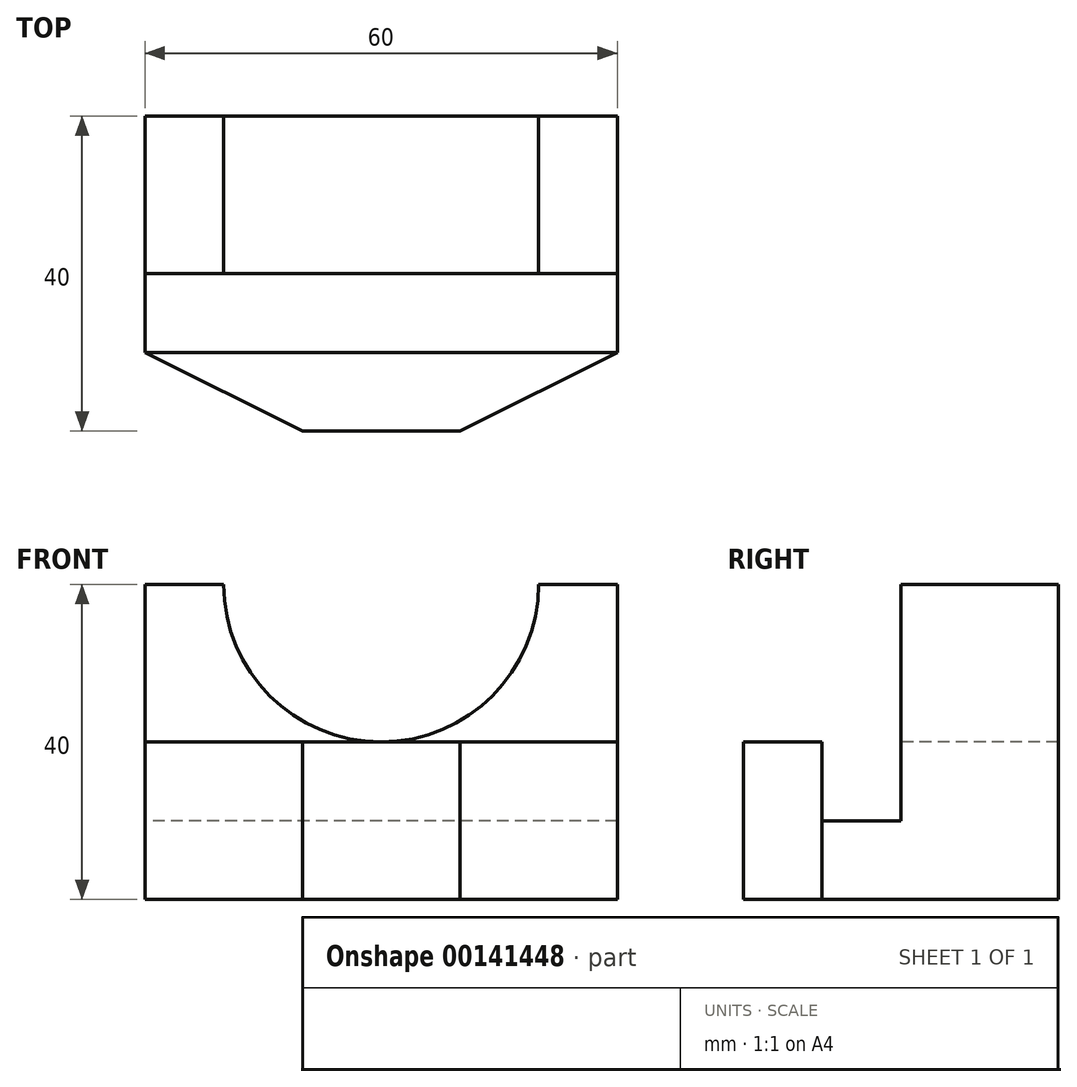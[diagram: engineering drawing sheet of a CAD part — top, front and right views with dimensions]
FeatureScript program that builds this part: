
annotation { "Feature Type Name" : "Feature", "Feature Type Description" : "" }
export const myFeature = defineFeature(function(context is Context, id is Id, definition is map)
    precondition{}
    {
        {
            var Q0;
            Q0=qCreatedBy(makeId("Front.planeOp"),FACE);
            var sketch = newSketch(context, id + "F0", { "sketchPlane" : qUnion([Q0])});
            skLineSegment(sketch, "E0.bottom", {"start": v(-30, 40) * mm, "end": v(30, 40) * mm});
            skLineSegment(sketch, "E0.top", {"start": v(-30, 0) * mm, "end": v(30, 0) * mm});
            skLineSegment(sketch, "E0.left", {"start": v(-30, 40) * mm, "end": v(-30, 0) * mm});
            skLineSegment(sketch, "E0.right", {"start": v(30, 40) * mm, "end": v(30, 0) * mm});
            skPoint(sketch, "E1", {"position": v(0, 40) * mm});
            skSolve(sketch);
        }
        {
            var Q0;
            Q0 = qSketchRegion(id + "F0", true);
            extrude(context, id + "F1", {"entities" : qUnion([Q0]), "oppositeDirection" : true, "depth" : 40 * mm});
        }
        {
            var Q0;
            Q0=makeQuery(id+"F1.opExtrude","SWEPT_FACE",FACE,{"disambiguationData":[OSD([sQuery(id+"F0.wireOp",EDGE,"E0.bottom")])]});
            var sketch = newSketch(context, id + "F2", { "sketchPlane" : qUnion([Q0])});
            skLineSegment(sketch, "E2", {"start": v(10, 0) * mm, "end": v(30, 10) * mm});
            skLineSegment(sketch, "E3", {"start": v(30, 10) * mm, "end": v(30, 0) * mm});
            skLineSegment(sketch, "E4", {"start": v(30, 0) * mm, "end": v(10, 0) * mm});
            skLineSegment(sketch, "E5", {"start": v(-30, 10) * mm, "end": v(-10, 0) * mm});
            skLineSegment(sketch, "E6", {"start": v(-10, 0) * mm, "end": v(-30, 0) * mm});
            skLineSegment(sketch, "E7", {"start": v(-30, 0) * mm, "end": v(-30, 10) * mm});
            skSolve(sketch);
        }
        {
            var Q0;
            Q0 = qSketchRegion(id + "F2", true);
            extrude(context, id + "F3", {"entities" : qUnion([Q0]), "operationType" : NewBodyOperationType.REMOVE, "endBound" : BoundingType.THROUGH_ALL, "oppositeDirection" : true, "depth" : 25 * mm});
        }
        {
            var Q0;
            Q0=makeQuery(id+"F1.opExtrude","SWEPT_FACE",FACE,{"disambiguationData":[OSD([sQuery(id+"F0.wireOp",EDGE,"E0.bottom")])]});
            var sketch = newSketch(context, id + "F4", { "sketchPlane" : qUnion([Q0])});
            skLineSegment(sketch, "E8", {"start": v(-30, 10) * mm, "end": v(-30, 20) * mm});
            skLineSegment(sketch, "E9", {"start": v(-30, 20) * mm, "end": v(30, 20) * mm});
            skLineSegment(sketch, "E10", {"start": v(30, 20) * mm, "end": v(30, 10) * mm});
            skLineSegment(sketch, "E11", {"start": v(30, 10) * mm, "end": v(-30, 10) * mm});
            skSolve(sketch);
        }
        {
            var Q0;
            Q0 = qSketchRegion(id + "F4", true);
            extrude(context, id + "F5", {"entities" : qUnion([Q0]), "operationType" : NewBodyOperationType.REMOVE, "oppositeDirection" : true, "depth" : 30 * mm});
        }
        {
            var Q0;
            Q0=qCreatedBy(makeId("Front.planeOp"),FACE);
            var sketch = newSketch(context, id + "F6", { "sketchPlane" : qUnion([Q0])});
            skArc(sketch, "E12", {"start": v(-20, 40) * mm, "mid": v(0, 20) * mm, "end": v(20, 40) * mm});
            skLineSegment(sketch, "E13", {"start": v(20, 40) * mm, "end": v(-20, 40) * mm});
            skSolve(sketch);
        }
        {
            var Q0;
            Q0 = qSketchRegion(id + "F6", true);
            extrude(context, id + "F7", {"entities" : qUnion([Q0]), "operationType" : NewBodyOperationType.REMOVE, "endBound" : BoundingType.THROUGH_ALL, "oppositeDirection" : true, "depth" : 25 * mm, "hasSecondDirection" : true, "secondDirectionBound" : SecondDirectionBoundingType.THROUGH_ALL, "secondDirectionOppositeDirection" : false, "secondDirectionDepth" : 25 * mm});
        }
        {
            var Q0;
            Q0=qCreatedBy(makeId("Right.planeOp"),FACE);
            var sketch = newSketch(context, id + "F8", { "sketchPlane" : qUnion([Q0])});
            skLineSegment(sketch, "E14", {"start": v(0, 20) * mm, "end": v(10, 20) * mm});
            skLineSegment(sketch, "E15", {"start": v(10, 20) * mm, "end": v(10, 40) * mm});
            skLineSegment(sketch, "E16", {"start": v(10, 40) * mm, "end": v(0, 40) * mm});
            skLineSegment(sketch, "E17", {"start": v(0, 40) * mm, "end": v(0, 20) * mm});
            skSolve(sketch);
        }
        {
            var Q0;
            Q0 = qSketchRegion(id + "F8", true);
            extrude(context, id + "F9", {"entities" : qUnion([Q0]), "operationType" : NewBodyOperationType.REMOVE, "endBound" : BoundingType.THROUGH_ALL, "oppositeDirection" : true, "depth" : 25 * mm, "hasSecondDirection" : true, "secondDirectionBound" : SecondDirectionBoundingType.THROUGH_ALL, "secondDirectionOppositeDirection" : false, "secondDirectionDepth" : 25 * mm});
        }
    });
